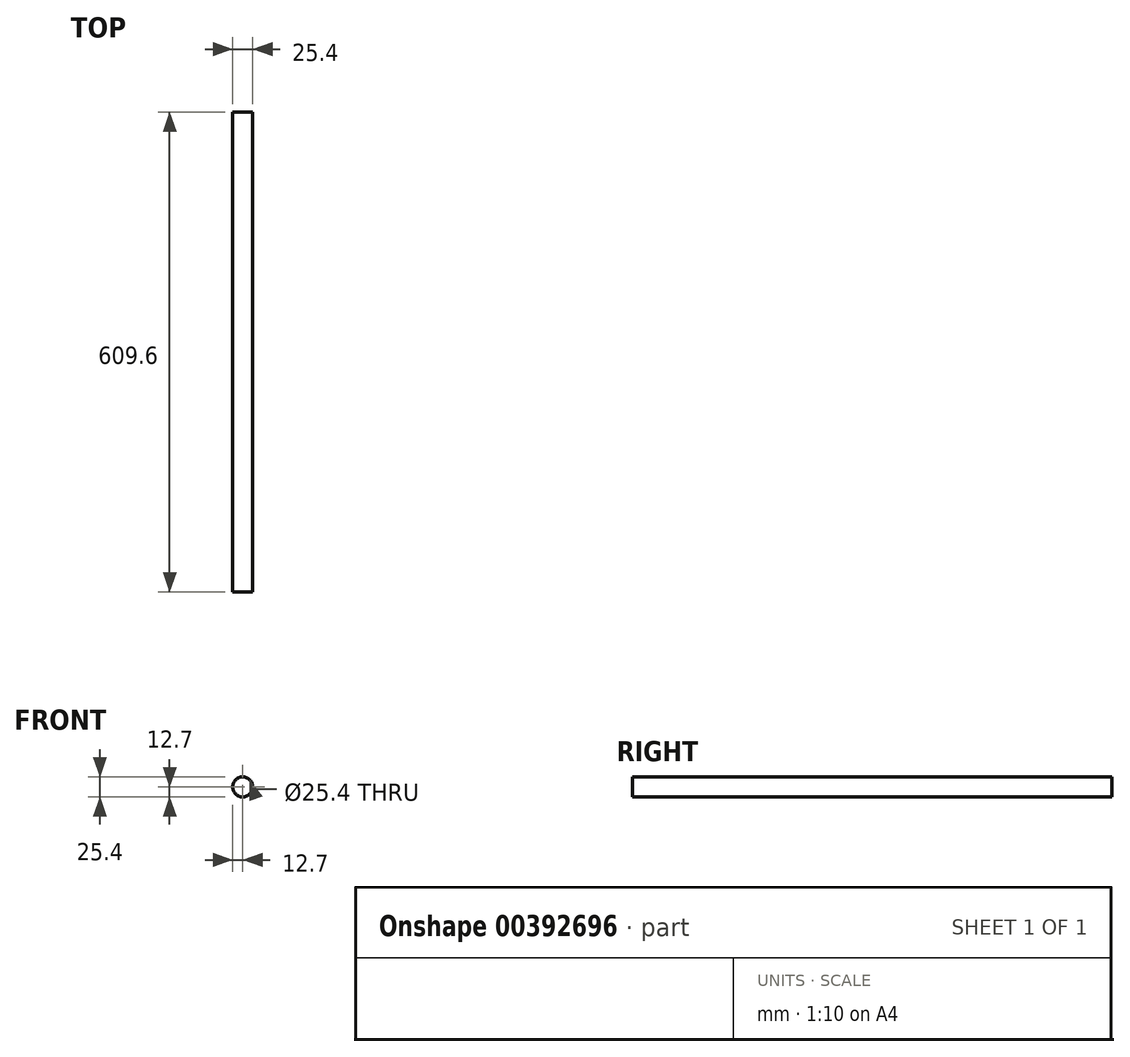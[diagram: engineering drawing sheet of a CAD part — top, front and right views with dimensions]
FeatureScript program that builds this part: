
annotation { "Feature Type Name" : "Feature", "Feature Type Description" : "" }
export const myFeature = defineFeature(function(context is Context, id is Id, definition is map)
    precondition{}
    {
        {
            var Q0;
            Q0=qCreatedBy(makeId("Front.planeOp"),FACE);
            var sketch = newSketch(context, id + "F0", { "sketchPlane" : qUnion([Q0])});
            skCircle(sketch, "E0", {"center": v(0, 0) * mm, "radius": 12.7 * mm});
            skSolve(sketch);
        }
        {
            var Q0;
            Q0=sQuery(id+"F0.wireOp",EDGE,"E0");
            var Q1;
            Q1=qCreatedBy(makeId("Front.planeOp"),FACE);
            extrude(context, id + "F1", {"bodyType" : ToolBodyType.SURFACE, "surfaceEntities" : qUnion([Q0]), "endBound" : BoundingType.SYMMETRIC, "oppositeDirection" : true, "endBoundEntityFace" : qUnion([Q1]), "depth" : 609.6 * mm});
        }
    });
